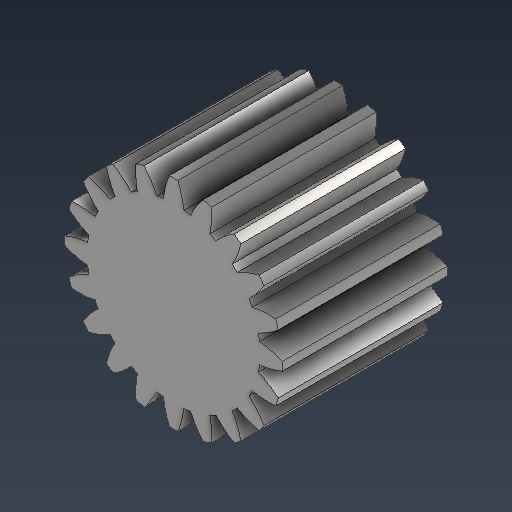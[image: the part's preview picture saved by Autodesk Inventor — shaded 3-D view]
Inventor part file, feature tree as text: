
AUTODESK INVENTOR PART (.ipt)
format: ipt  version: 2021 (Build 250183000, 183)  size: 292,352 bytes
history: native  units: mm (DEFAULTED — no unit token found)
features: plane x3, other x3, sketch x2, extrude x1
ambient origin geometry x8: Origin, YZ Plane, XZ Plane, XY Plane, X Axis, Y Axis, Z Axis, Center Point
bodies: Solid1 (feature_tree)
feature tree (9):
  extrude  "Extrusion1"  Depth=1.5mm TaperAngle=0.0deg
  plane  "Work Plane2"
  plane  "Work Plane8"
  plane  "Work Plane9"
  other  "Engrenagem reta"
  sketch  "Sketch1"  dims[d0=1.979995mm d1=1.5mm d2=0.0mm]
  sketch  "Sketch2"  dims[d3=1.8mm d4=10.0mm d5=0.0mm d16=3.597721mm d17=0.0mm d34=1.570796mm d39=0.0mm d41=0.0mm d43=3.597721mm d46=3.597721mm d47=0.0mm d48=0.0mm]
  other  "Srf1"
  other  "Diâmetro do flanco"
